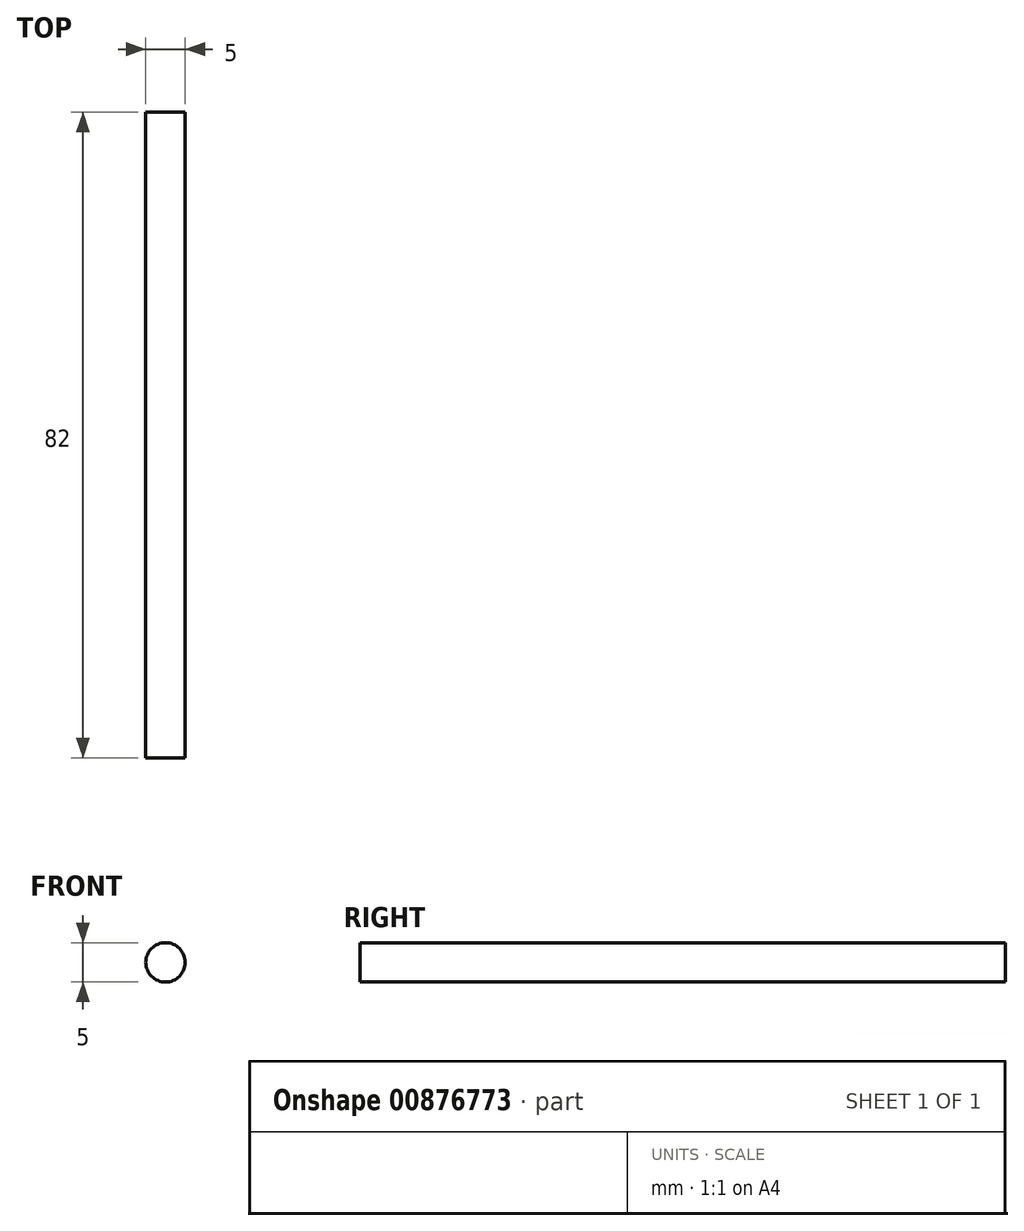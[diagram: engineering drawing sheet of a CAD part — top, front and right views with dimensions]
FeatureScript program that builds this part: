
annotation { "Feature Type Name" : "Feature", "Feature Type Description" : "" }
export const myFeature = defineFeature(function(context is Context, id is Id, definition is map)
    precondition{}
    {
        {
            var Q0;
            Q0=qCreatedBy(makeId("Front.planeOp"),FACE);
            var sketch = newSketch(context, id + "F0", { "sketchPlane" : qUnion([Q0])});
            skCircle(sketch, "E0", {"center": v(0, 0) * mm, "radius": 2.5 * mm});
            skSolve(sketch);
        }
        {
            var Q0;
            Q0=qSketchRegion(id+"F0",true);
            extrude(context, id + "F1", {"entities" : qUnion([Q0]), "depth" : 82 * mm, "offsetDistance" : 25 * mm});
        }
    });
